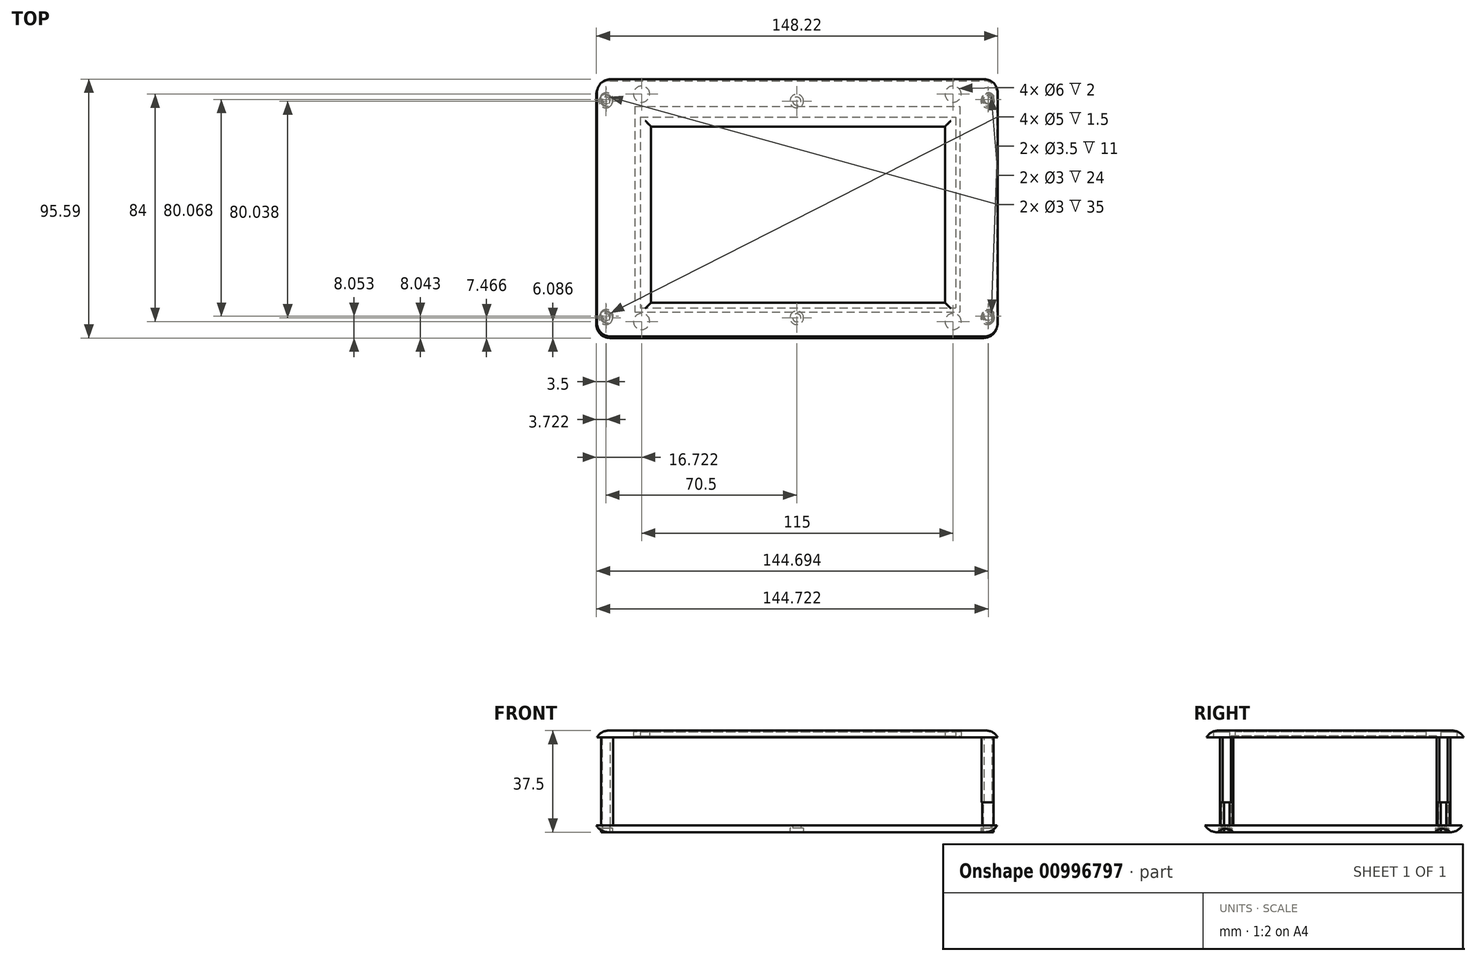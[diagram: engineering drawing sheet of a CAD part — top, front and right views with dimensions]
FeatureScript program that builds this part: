
annotation { "Feature Type Name" : "Feature", "Feature Type Description" : "" }
export const myFeature = defineFeature(function(context is Context, id is Id, definition is map)
    precondition{}
    {
        {
            var Q0;
            Q0=qCreatedBy(makeId("Top.planeOp"),FACE);
            var sketch = newSketch(context, id + "F0", { "sketchPlane" : qUnion([Q0])});
            skLineSegment(sketch, "E0.bottom", {"start": v(-66.78, 48.09) * mm, "end": v(67.22, 48.09) * mm});
            skLineSegment(sketch, "E0.top", {"start": v(-66.78, -46.91) * mm, "end": v(67.22, -46.91) * mm});
            skLineSegment(sketch, "E0.left", {"start": v(-66.78, 48.09) * mm, "end": v(-66.78, -46.91) * mm});
            skLineSegment(sketch, "E0.right", {"start": v(67.22, 48.09) * mm, "end": v(67.22, -46.91) * mm});
            skPoint(sketch, "E0.middle", {"position": v(0.22, 0.59) * mm});
            skLineSegment(sketch, "E1.bottom", {"start": v(-59.78, 38.09) * mm, "end": v(60.22, 38.09) * mm});
            skLineSegment(sketch, "E1.top", {"start": v(-59.78, -37.91) * mm, "end": v(60.22, -37.91) * mm});
            skLineSegment(sketch, "E1.left", {"start": v(-59.78, 38.09) * mm, "end": v(-59.78, -37.91) * mm});
            skLineSegment(sketch, "E1.right", {"start": v(60.22, 38.09) * mm, "end": v(60.22, -37.91) * mm});
            skPoint(sketch, "E2.visualSharp", {"position": v(-66.78, 48.09) * mm});
            skLineSegment(sketch, "E2.filletArc", {"start": v(-66.78, 48.09) * mm, "end": v(-66.78, 48.09) * mm});
            skPoint(sketch, "E3.visualSharp", {"position": v(67.22, 48.09) * mm});
            skLineSegment(sketch, "E3.filletArc", {"start": v(67.22, 48.09) * mm, "end": v(67.22, 48.09) * mm});
            skPoint(sketch, "E4.visualSharp", {"position": v(67.22, -46.91) * mm});
            skLineSegment(sketch, "E4.filletArc", {"start": v(67.22, -46.91) * mm, "end": v(67.22, -46.91) * mm});
            skPoint(sketch, "E5.visualSharp", {"position": v(-66.78, -46.91) * mm});
            skLineSegment(sketch, "E5.filletArc", {"start": v(-66.78, -46.91) * mm, "end": v(-66.78, -46.91) * mm});
            skLineSegment(sketch, "E6.bottom", {"start": v(-57.78, 34.09) * mm, "end": v(58.72, 34.09) * mm});
            skLineSegment(sketch, "E6.top", {"start": v(-57.78, -36.41) * mm, "end": v(58.72, -36.41) * mm});
            skLineSegment(sketch, "E6.left", {"start": v(-57.78, 34.09) * mm, "end": v(-57.78, -36.41) * mm});
            skLineSegment(sketch, "E6.right", {"start": v(58.72, 34.09) * mm, "end": v(58.72, -36.41) * mm});
            skLineSegment(sketch, "E7.bottom", {"start": v(-53.78, 30.59) * mm, "end": v(54.72, 30.59) * mm});
            skLineSegment(sketch, "E7.top", {"start": v(-53.78, -34.41) * mm, "end": v(54.72, -34.41) * mm});
            skLineSegment(sketch, "E7.left", {"start": v(-53.78, 30.59) * mm, "end": v(-53.78, -34.41) * mm});
            skLineSegment(sketch, "E7.right", {"start": v(54.72, 30.59) * mm, "end": v(54.72, -34.41) * mm});
            skCircle(sketch, "E8", {"center": v(57.72, -41.41) * mm, "radius": 3 * mm});
            skCircle(sketch, "E9", {"center": v(57.72, 42.59) * mm, "radius": 3 * mm});
            skCircle(sketch, "E10", {"center": v(-57.28, 42.59) * mm, "radius": 3 * mm});
            skCircle(sketch, "E11", {"center": v(-57.28, -41.41) * mm, "radius": 3 * mm});
            skLineSegment(sketch, "E12.bottom", {"start": v(-66.78, -46.91) * mm, "end": v(-68.78, -46.91) * mm});
            skLineSegment(sketch, "E12.top", {"start": v(-66.78, 48.09) * mm, "end": v(-68.78, 48.09) * mm});
            skLineSegment(sketch, "E12.left", {"start": v(-66.78, -46.91) * mm, "end": v(-66.78, 48.09) * mm});
            skLineSegment(sketch, "E12.right", {"start": v(-73.78, -41.91) * mm, "end": v(-73.78, 43.09) * mm});
            skLineSegment(sketch, "E13.bottom", {"start": v(67.22, -46.91) * mm, "end": v(69.22, -46.91) * mm});
            skLineSegment(sketch, "E13.top", {"start": v(67.22, 48.09) * mm, "end": v(69.22, 48.09) * mm});
            skLineSegment(sketch, "E13.left", {"start": v(67.22, -46.91) * mm, "end": v(67.22, 48.09) * mm});
            skLineSegment(sketch, "E13.right", {"start": v(74.22, -41.91) * mm, "end": v(74.22, 43.09) * mm});
            skPoint(sketch, "E14.visualSharp", {"position": v(-73.78, 48.09) * mm});
            skArc(sketch, "E14.filletArc", {"start": v(-68.78, 48.09) * mm, "mid": v(-72.31, 46.62) * mm, "end": v(-73.78, 43.09) * mm});
            skPoint(sketch, "E15.visualSharp", {"position": v(74.22, 48.09) * mm});
            skArc(sketch, "E15.filletArc", {"start": v(74.22, 43.09) * mm, "mid": v(72.76, 46.62) * mm, "end": v(69.22, 48.09) * mm});
            skPoint(sketch, "E16.visualSharp", {"position": v(74.22, -46.91) * mm});
            skArc(sketch, "E16.filletArc", {"start": v(69.22, -46.91) * mm, "mid": v(72.76, -45.45) * mm, "end": v(74.22, -41.91) * mm});
            skPoint(sketch, "E17.visualSharp", {"position": v(-73.78, -46.91) * mm});
            skArc(sketch, "E17.filletArc", {"start": v(-73.78, -41.91) * mm, "mid": v(-72.31, -45.45) * mm, "end": v(-68.78, -46.91) * mm});
            skArc(sketch, "E18", {"start": v(-72.28, 39.1) * mm, "mid": v(-67.78, 40.6) * mm, "end": v(-72.28, 42.1) * mm});
            skCircle(sketch, "E19", {"center": v(-70.28, 40.6) * mm, "radius": 1.5 * mm});
            skArc(sketch, "E20", {"start": v(-72.28, -40.95) * mm, "mid": v(-67.78, -39.45) * mm, "end": v(-72.28, -37.95) * mm});
            skCircle(sketch, "E21", {"center": v(-70.28, -39.45) * mm, "radius": 1.5 * mm});
            skArc(sketch, "E22", {"start": v(72.72, -37.95) * mm, "mid": v(68.22, -39.45) * mm, "end": v(72.72, -40.95) * mm});
            skCircle(sketch, "E23", {"center": v(70.72, -39.45) * mm, "radius": 1.5 * mm});
            skArc(sketch, "E24", {"start": v(72.72, 42.1) * mm, "mid": v(68.22, 40.6) * mm, "end": v(72.72, 39.1) * mm});
            skCircle(sketch, "E25", {"center": v(70.72, 40.6) * mm, "radius": 1.5 * mm});
            skLineSegment(sketch, "E26", {"start": v(-72.28, 42.1) * mm, "end": v(-72.28, 39.1) * mm});
            skLineSegment(sketch, "E27.trimOffspring", {"start": v(-72.28, -37.95) * mm, "end": v(-72.28, -40.95) * mm});
            skLineSegment(sketch, "E28", {"start": v(72.72, 42.1) * mm, "end": v(72.72, 39.1) * mm});
            skLineSegment(sketch, "E29.trimOffspring", {"start": v(72.72, -37.95) * mm, "end": v(72.72, -40.95) * mm});
            skSolve(sketch);
        }
        {
            var Q0;
            Q0 = qSketchRegion(id + "F0", true);
            var Q1;
            Q1=makeQuery(id+"F0.imprint","IMPRINT",FACE,{"disambiguationData":[TD([[makeQuery(id+"F0.imprint","IMPRINT",EDGE,{"derivedFrom":sQuery(id+"F0.wireOp",EDGE,"E10")}),1.0]])]});
            var Q2;
            Q2=makeQuery(id+"F0.imprint","IMPRINT",FACE,{"disambiguationData":[TD([[makeQuery(id+"F0.imprint","IMPRINT",EDGE,{"derivedFrom":sQuery(id+"F0.wireOp",EDGE,"E9")}),1.0]])]});
            var Q3;
            Q3=makeQuery(id+"F0.imprint","IMPRINT",FACE,{"disambiguationData":[TD([[makeQuery(id+"F0.imprint","IMPRINT",EDGE,{"derivedFrom":sQuery(id+"F0.wireOp",EDGE,"E8")}),1.0]])]});
            var Q4;
            Q4=makeQuery(id+"F0.imprint","IMPRINT",FACE,{"disambiguationData":[TD([[makeQuery(id+"F0.imprint","IMPRINT",EDGE,{"derivedFrom":sQuery(id+"F0.wireOp",EDGE,"E11")}),1.0]])]});
            var Q5;
            Q5=makeQuery(id+"F0.imprint","IMPRINT",FACE,{"disambiguationData":[TD([[makeQuery(id+"F0.imprint","IMPRINT",EDGE,{"derivedFrom":sQuery(id+"F0.wireOp",EDGE,"E1.bottom")}),-1.0]])]});
            var Q6;
            Q6=makeQuery(id+"F0.imprint","IMPRINT",FACE,{"disambiguationData":[TD([[makeQuery(id+"F0.imprint","IMPRINT",EDGE,{"derivedFrom":sQuery(id+"F0.wireOp",EDGE,"E6.bottom")}),-1.0]])]});
            var Q7;
            Q7=makeQuery(id+"F0.imprint","IMPRINT",FACE,{"disambiguationData":[TD([[makeQuery(id+"F0.imprint","IMPRINT",EDGE,{"derivedFrom":sQuery(id+"F0.wireOp",EDGE,"E18")}),1.0]])]});
            var Q8;
            Q8=makeQuery(id+"F0.imprint","IMPRINT",FACE,{"disambiguationData":[TD([[makeQuery(id+"F0.imprint","IMPRINT",EDGE,{"derivedFrom":sQuery(id+"F0.wireOp",EDGE,"E19")}),1.0]])]});
            var Q9;
            Q9=makeQuery(id+"F0.imprint","IMPRINT",FACE,{"disambiguationData":[TD([[makeQuery(id+"F0.imprint","IMPRINT",EDGE,{"derivedFrom":sQuery(id+"F0.wireOp",EDGE,"E20")}),1.0]])]});
            var Q10;
            Q10=makeQuery(id+"F0.imprint","IMPRINT",FACE,{"disambiguationData":[TD([[makeQuery(id+"F0.imprint","IMPRINT",EDGE,{"derivedFrom":sQuery(id+"F0.wireOp",EDGE,"E21")}),1.0]])]});
            var Q11;
            Q11=makeQuery(id+"F0.imprint","IMPRINT",FACE,{"disambiguationData":[TD([[makeQuery(id+"F0.imprint","IMPRINT",EDGE,{"derivedFrom":sQuery(id+"F0.wireOp",EDGE,"E22")}),1.0]])]});
            var Q12;
            Q12=makeQuery(id+"F0.imprint","IMPRINT",FACE,{"disambiguationData":[TD([[makeQuery(id+"F0.imprint","IMPRINT",EDGE,{"derivedFrom":sQuery(id+"F0.wireOp",EDGE,"E23")}),1.0]])]});
            var Q13;
            Q13=makeQuery(id+"F0.imprint","IMPRINT",FACE,{"disambiguationData":[TD([[makeQuery(id+"F0.imprint","IMPRINT",EDGE,{"derivedFrom":sQuery(id+"F0.wireOp",EDGE,"E24")}),1.0]])]});
            var Q14;
            Q14=makeQuery(id+"F0.imprint","IMPRINT",FACE,{"disambiguationData":[TD([[makeQuery(id+"F0.imprint","IMPRINT",EDGE,{"derivedFrom":sQuery(id+"F0.wireOp",EDGE,"E25")}),1.0]])]});
            extrude(context, id + "F1", {"entities" : qUnion([Q0, Q1, Q2, Q3, Q4, Q5, Q6, Q7, Q8, Q9, Q10, Q11, Q12, Q13, Q14]), "depth" : 2.5 * mm, "offsetDistance" : 25 * mm});
        }
        {
            var Q0;
            Q0=makeQuery(id+"F0.imprint","IMPRINT",FACE,{"disambiguationData":[TD([[makeQuery(id+"F0.imprint","IMPRINT",EDGE,{"derivedFrom":sQuery(id+"F0.wireOp",EDGE,"E10")}),1.0]])]});
            var Q1;
            Q1=makeQuery(id+"F0.imprint","IMPRINT",FACE,{"disambiguationData":[TD([[makeQuery(id+"F0.imprint","IMPRINT",EDGE,{"derivedFrom":sQuery(id+"F0.wireOp",EDGE,"E11")}),1.0]])]});
            var Q2;
            Q2=makeQuery(id+"F0.imprint","IMPRINT",FACE,{"disambiguationData":[TD([[makeQuery(id+"F0.imprint","IMPRINT",EDGE,{"derivedFrom":sQuery(id+"F0.wireOp",EDGE,"E8")}),1.0]])]});
            var Q3;
            Q3=makeQuery(id+"F0.imprint","IMPRINT",FACE,{"disambiguationData":[TD([[makeQuery(id+"F0.imprint","IMPRINT",EDGE,{"derivedFrom":sQuery(id+"F0.wireOp",EDGE,"E9")}),1.0]])]});
            var Q4;
            Q4=makeQuery(id+"F0.imprint","IMPRINT",FACE,{"disambiguationData":[TD([[makeQuery(id+"F0.imprint","IMPRINT",EDGE,{"derivedFrom":sQuery(id+"F0.wireOp",EDGE,"E6.bottom")}),-1.0]])]});
            extrude(context, id + "F2", {"entities" : qUnion([Q0, Q1, Q2, Q3, Q4]), "operationType" : NewBodyOperationType.REMOVE, "depth" : 2 * mm, "offsetDistance" : 25 * mm});
        }
        {
            var Q0;
            Q0=makeQuery(id+"F0.imprint","IMPRINT",FACE,{"disambiguationData":[TD([[makeQuery(id+"F0.imprint","IMPRINT",EDGE,{"derivedFrom":sQuery(id+"F0.wireOp",EDGE,"E1.bottom")}),-1.0]])]});
            extrude(context, id + "F3", {"entities" : qUnion([Q0]), "operationType" : NewBodyOperationType.REMOVE, "depth" : .5 * mm, "offsetDistance" : 25 * mm});
        }
        {
            var Q0;
            Q0=makeQuery(id+"F1.opExtrude","CAP_EDGE",EDGE,{"disambiguationData":[OSD([sQuery(id+"F0.wireOp",EDGE,"E7.bottom")])],"isStart":false});
            var Q1;
            Q1=makeQuery(id+"F1.opExtrude","CAP_EDGE",EDGE,{"disambiguationData":[OSD([sQuery(id+"F0.wireOp",EDGE,"E7.left")])],"isStart":false});
            var Q2;
            Q2=makeQuery(id+"F1.opExtrude","CAP_EDGE",EDGE,{"disambiguationData":[OSD([sQuery(id+"F0.wireOp",EDGE,"E7.top")])],"isStart":false});
            var Q3;
            Q3=makeQuery(id+"F1.opExtrude","CAP_EDGE",EDGE,{"disambiguationData":[OSD([sQuery(id+"F0.wireOp",EDGE,"E7.right")])],"isStart":false});
            var Q4;
            Q4=makeQuery(id+"F1.opExtrude","CAP_EDGE",EDGE,{"disambiguationData":[OSD([sQuery(id+"F0.wireOp",EDGE,"E13.right")])],"isStart":false});
            var Q5;
            Q5=makeQuery(id+"F1.opExtrude","CAP_EDGE",EDGE,{"disambiguationData":[OSD([sQuery(id+"F0.wireOp",EDGE,"E15.filletArc")])],"isStart":false});
            var Q6;
            Q6=makeQuery(id+"F1.opExtrude","CAP_EDGE",EDGE,{"disambiguationData":[OSD([sQuery(id+"F0.wireOp",EDGE,"E0.bottom"),sQuery(id+"F0.wireOp",EDGE,"E12.top"),sQuery(id+"F0.wireOp",EDGE,"E13.top")])],"isStart":false});
            var Q7;
            Q7=makeQuery(id+"F1.opExtrude","CAP_EDGE",EDGE,{"disambiguationData":[OSD([sQuery(id+"F0.wireOp",EDGE,"E0.top"),sQuery(id+"F0.wireOp",EDGE,"E12.bottom"),sQuery(id+"F0.wireOp",EDGE,"E13.bottom")])],"isStart":false});
            var Q8;
            Q8=makeQuery(id+"F1.opExtrude","CAP_EDGE",EDGE,{"disambiguationData":[OSD([sQuery(id+"F0.wireOp",EDGE,"E16.filletArc")])],"isStart":false});
            var Q9;
            Q9=makeQuery(id+"F1.opExtrude","CAP_EDGE",EDGE,{"disambiguationData":[OSD([sQuery(id+"F0.wireOp",EDGE,"E17.filletArc")])],"isStart":false});
            var Q10;
            Q10=makeQuery(id+"F1.opExtrude","CAP_EDGE",EDGE,{"disambiguationData":[OSD([sQuery(id+"F0.wireOp",EDGE,"E12.right")])],"isStart":false});
            var Q11;
            Q11=makeQuery(id+"F1.opExtrude","CAP_EDGE",EDGE,{"disambiguationData":[OSD([sQuery(id+"F0.wireOp",EDGE,"E14.filletArc")])],"isStart":false});
            fillet(context, id + "F4", {"entities" : qUnion([Q0, Q1, Q2, Q3, Q4, Q5, Q6, Q7, Q8, Q9, Q10, Q11]), "radius" : 5 * mm, "allowEdgeOverflow" : false});
        }
        {
            var Q0;
            Q0=makeQuery(id+"F0.imprint","IMPRINT",FACE,{"disambiguationData":[TD([[makeQuery(id+"F0.imprint","IMPRINT",EDGE,{"derivedFrom":sQuery(id+"F0.wireOp",EDGE,"E18")}),1.0]])]});
            var Q1;
            Q1=makeQuery(id+"F0.imprint","IMPRINT",FACE,{"disambiguationData":[TD([[makeQuery(id+"F0.imprint","IMPRINT",EDGE,{"derivedFrom":sQuery(id+"F0.wireOp",EDGE,"E20")}),1.0]])]});
            extrude(context, id + "F5", {"entities" : qUnion([Q0, Q1]), "operationType" : NewBodyOperationType.ADD, "oppositeDirection" : true, "depth" : 35 * mm, "offsetDistance" : 25 * mm});
        }
        {
            var Q0;
            Q0=makeQuery(id+"F0.imprint","IMPRINT",FACE,{"disambiguationData":[TD([[makeQuery(id+"F0.imprint","IMPRINT",EDGE,{"derivedFrom":sQuery(id+"F0.wireOp",EDGE,"E24")}),1.0]])]});
            var Q1;
            Q1=makeQuery(id+"F0.imprint","IMPRINT",FACE,{"disambiguationData":[TD([[makeQuery(id+"F0.imprint","IMPRINT",EDGE,{"derivedFrom":sQuery(id+"F0.wireOp",EDGE,"E22")}),1.0]])]});
            extrude(context, id + "F6", {"entities" : qUnion([Q0, Q1]), "operationType" : NewBodyOperationType.ADD, "oppositeDirection" : true, "depth" : 24 * mm, "offsetDistance" : 25 * mm});
        }
        {
            var Q0;
            Q0=qCreatedBy(makeId("Top.planeOp"),FACE);
            cPlane(context, id + "F7", {"entities" : qUnion([Q0]), "cplaneType" : CPlaneType.OFFSET, "offset" : 35 * mm, "oppositeDirection" : true, "width" : 150 * mm, "height" : 150 * mm});
        }
        {
            var Q0;
            Q0=qCreatedBy(id+"F7.planeOp",FACE);
            var sketch = newSketch(context, id + "F8", { "sketchPlane" : qUnion([Q0])});
            skLineSegment(sketch, "E30.bottom", {"start": v(-69, -47.5) * mm, "end": v(69, -47.5) * mm});
            skLineSegment(sketch, "E30.top", {"start": v(-69, 47.5) * mm, "end": v(69, 47.5) * mm});
            skLineSegment(sketch, "E30.left", {"start": v(-74, -42.5) * mm, "end": v(-74, 42.5) * mm});
            skLineSegment(sketch, "E30.right", {"start": v(74, -42.5) * mm, "end": v(74, 42.5) * mm});
            skPoint(sketch, "E30.middle", {"position": v(0, 0) * mm});
            skPoint(sketch, "E31.visualSharp", {"position": v(-74, -47.5) * mm});
            skArc(sketch, "E31.filletArc", {"start": v(-74, -42.5) * mm, "mid": v(-72.54, -46.04) * mm, "end": v(-69, -47.5) * mm});
            skPoint(sketch, "E32.visualSharp", {"position": v(-74, 47.5) * mm});
            skArc(sketch, "E32.filletArc", {"start": v(-69, 47.5) * mm, "mid": v(-72.54, 46.04) * mm, "end": v(-74, 42.5) * mm});
            skPoint(sketch, "E33.visualSharp", {"position": v(74, -47.5) * mm});
            skArc(sketch, "E33.filletArc", {"start": v(69, -47.5) * mm, "mid": v(72.54, -46.04) * mm, "end": v(74, -42.5) * mm});
            skPoint(sketch, "E34.visualSharp", {"position": v(74, 47.5) * mm});
            skArc(sketch, "E34.filletArc", {"start": v(74, 42.5) * mm, "mid": v(72.54, 46.04) * mm, "end": v(69, 47.5) * mm});
            skCircle(sketch, "E35", {"center": v(-70.5, 40) * mm, "radius": 1.5 * mm});
            skCircle(sketch, "E36", {"center": v(-70.5, -40.03) * mm, "radius": 1.5 * mm});
            skCircle(sketch, "E37", {"center": v(70.5, -40.03) * mm, "radius": 1.5 * mm});
            skCircle(sketch, "E38", {"center": v(70.5, 40) * mm, "radius": 1.5 * mm});
            skCircle(sketch, "E39", {"center": v(0, -40.03) * mm, "radius": 1.5 * mm});
            skCircle(sketch, "E40", {"center": v(0, 40) * mm, "radius": 1.5 * mm});
            skCircle(sketch, "E41", {"center": v(-70.5, 40) * mm, "radius": 2.5 * mm});
            skCircle(sketch, "E42", {"center": v(-70.5, -40.03) * mm, "radius": 2.5 * mm});
            skCircle(sketch, "E43", {"center": v(0, -40.03) * mm, "radius": 2.5 * mm});
            skCircle(sketch, "E44", {"center": v(70.5, -40.03) * mm, "radius": 2.5 * mm});
            skCircle(sketch, "E45", {"center": v(70.5, 40) * mm, "radius": 2.5 * mm});
            skCircle(sketch, "E46", {"center": v(0, 40) * mm, "radius": 2.5 * mm});
            skSolve(sketch);
        }
        {
            var Q0;
            Q0=makeQuery(id+"F8.imprint","IMPRINT",FACE,{"disambiguationData":[TD([[makeQuery(id+"F8.imprint","IMPRINT",EDGE,{"derivedFrom":sQuery(id+"F8.wireOp",EDGE,"E30.bottom")}),1.0]])]});
            var Q1;
            Q1=makeQuery(id+"F8.imprint","IMPRINT",FACE,{"disambiguationData":[TD([[makeQuery(id+"F8.imprint","IMPRINT",EDGE,{"derivedFrom":sQuery(id+"F8.wireOp",EDGE,"E35")}),-1.0]])]});
            var Q2;
            Q2=makeQuery(id+"F8.imprint","IMPRINT",FACE,{"disambiguationData":[TD([[makeQuery(id+"F8.imprint","IMPRINT",EDGE,{"derivedFrom":sQuery(id+"F8.wireOp",EDGE,"E36")}),-1.0]])]});
            var Q3;
            Q3=makeQuery(id+"F8.imprint","IMPRINT",FACE,{"disambiguationData":[TD([[makeQuery(id+"F8.imprint","IMPRINT",EDGE,{"derivedFrom":sQuery(id+"F8.wireOp",EDGE,"E40")}),-1.0]])]});
            var Q4;
            Q4=makeQuery(id+"F8.imprint","IMPRINT",FACE,{"disambiguationData":[TD([[makeQuery(id+"F8.imprint","IMPRINT",EDGE,{"derivedFrom":sQuery(id+"F8.wireOp",EDGE,"E39")}),-1.0]])]});
            var Q5;
            Q5=makeQuery(id+"F8.imprint","IMPRINT",FACE,{"disambiguationData":[TD([[makeQuery(id+"F8.imprint","IMPRINT",EDGE,{"derivedFrom":sQuery(id+"F8.wireOp",EDGE,"E38")}),-1.0]])]});
            var Q6;
            Q6=makeQuery(id+"F8.imprint","IMPRINT",FACE,{"disambiguationData":[TD([[makeQuery(id+"F8.imprint","IMPRINT",EDGE,{"derivedFrom":sQuery(id+"F8.wireOp",EDGE,"E37")}),-1.0]])]});
            extrude(context, id + "F9", {"entities" : qUnion([Q0, Q1, Q2, Q3, Q4, Q5, Q6]), "depth" : 2.5 * mm, "offsetDistance" : 25 * mm});
        }
        {
            var Q0;
            Q0=makeQuery(id+"F9.opExtrude","CAP_EDGE",EDGE,{"disambiguationData":[OSD([sQuery(id+"F8.wireOp",EDGE,"E30.left")])],"isStart":true});
            fillet(context, id + "F10", {"entities" : qUnion([Q0]), "radius" : 5 * mm, "tangentPropagation" : true, "allowEdgeOverflow" : false});
        }
        {
            var Q0;
            Q0=makeQuery(id+"F8.imprint","IMPRINT",FACE,{"disambiguationData":[TD([[makeQuery(id+"F8.imprint","IMPRINT",EDGE,{"derivedFrom":sQuery(id+"F8.wireOp",EDGE,"E35")}),-1.0]])]});
            var Q1;
            Q1=makeQuery(id+"F8.imprint","IMPRINT",FACE,{"disambiguationData":[TD([[makeQuery(id+"F8.imprint","IMPRINT",EDGE,{"derivedFrom":sQuery(id+"F8.wireOp",EDGE,"E36")}),-1.0]])]});
            var Q2;
            Q2=makeQuery(id+"F8.imprint","IMPRINT",FACE,{"disambiguationData":[TD([[makeQuery(id+"F8.imprint","IMPRINT",EDGE,{"derivedFrom":sQuery(id+"F8.wireOp",EDGE,"E39")}),-1.0]])]});
            var Q3;
            Q3=makeQuery(id+"F8.imprint","IMPRINT",FACE,{"disambiguationData":[TD([[makeQuery(id+"F8.imprint","IMPRINT",EDGE,{"derivedFrom":sQuery(id+"F8.wireOp",EDGE,"E40")}),-1.0]])]});
            var Q4;
            Q4=makeQuery(id+"F8.imprint","IMPRINT",FACE,{"disambiguationData":[TD([[makeQuery(id+"F8.imprint","IMPRINT",EDGE,{"derivedFrom":sQuery(id+"F8.wireOp",EDGE,"E38")}),-1.0]])]});
            var Q5;
            Q5=makeQuery(id+"F8.imprint","IMPRINT",FACE,{"disambiguationData":[TD([[makeQuery(id+"F8.imprint","IMPRINT",EDGE,{"derivedFrom":sQuery(id+"F8.wireOp",EDGE,"E37")}),-1.0]])]});
            extrude(context, id + "F11", {"entities" : qUnion([Q0, Q1, Q2, Q3, Q4, Q5]), "operationType" : NewBodyOperationType.REMOVE, "depth" : 1.5 * mm, "offsetDistance" : 25 * mm});
        }
        {
            var Q0;
            Q0=makeQuery(id+"F0.imprint","IMPRINT",FACE,{"disambiguationData":[TD([[makeQuery(id+"F0.imprint","IMPRINT",EDGE,{"derivedFrom":sQuery(id+"F0.wireOp",EDGE,"E7.bottom")}),-1.0]])]});
            cPlane(context, id + "F12", {"entities" : qUnion([Q0]), "cplaneType" : CPlaneType.OFFSET, "offset" : 24 * mm, "oppositeDirection" : true, "width" : 150 * mm, "height" : 150 * mm});
        }
        {
            var Q0;
            Q0=qCreatedBy(id+"F12.planeOp",FACE);
            var sketch = newSketch(context, id + "F13", { "sketchPlane" : qUnion([Q0])});
            skArc(sketch, "E47", {"start": v(72.7, 41.64) * mm, "mid": v(68.44, 40.61) * mm, "end": v(72.7, 39.58) * mm});
            skCircle(sketch, "E48", {"center": v(70.7, 40.61) * mm, "radius": 1.75 * mm});
            skLineSegment(sketch, "E49", {"start": v(72.7, 41.64) * mm, "end": v(72.7, 39.58) * mm});
            skArc(sketch, "E50", {"start": v(72.7, -38.43) * mm, "mid": v(68.44, -39.46) * mm, "end": v(72.7, -40.49) * mm});
            skCircle(sketch, "E51", {"center": v(70.7, -39.46) * mm, "radius": 1.75 * mm});
            skLineSegment(sketch, "E52", {"start": v(72.7, -38.43) * mm, "end": v(72.7, -40.49) * mm});
            skSolve(sketch);
        }
        {
            var Q0;
            Q0=makeQuery(id+"F13.imprint","IMPRINT",FACE,{"disambiguationData":[TD([[makeQuery(id+"F13.imprint","IMPRINT",EDGE,{"derivedFrom":sQuery(id+"F13.wireOp",EDGE,"E47")}),1.0]])]});
            var Q1;
            Q1=makeQuery(id+"F13.imprint","IMPRINT",FACE,{"disambiguationData":[TD([[makeQuery(id+"F13.imprint","IMPRINT",EDGE,{"derivedFrom":sQuery(id+"F13.wireOp",EDGE,"E50")}),1.0]])]});
            extrude(context, id + "F14", {"entities" : qUnion([Q0, Q1]), "operationType" : NewBodyOperationType.ADD, "oppositeDirection" : true, "depth" : 11 * mm, "offsetDistance" : 25 * mm});
        }
    });
